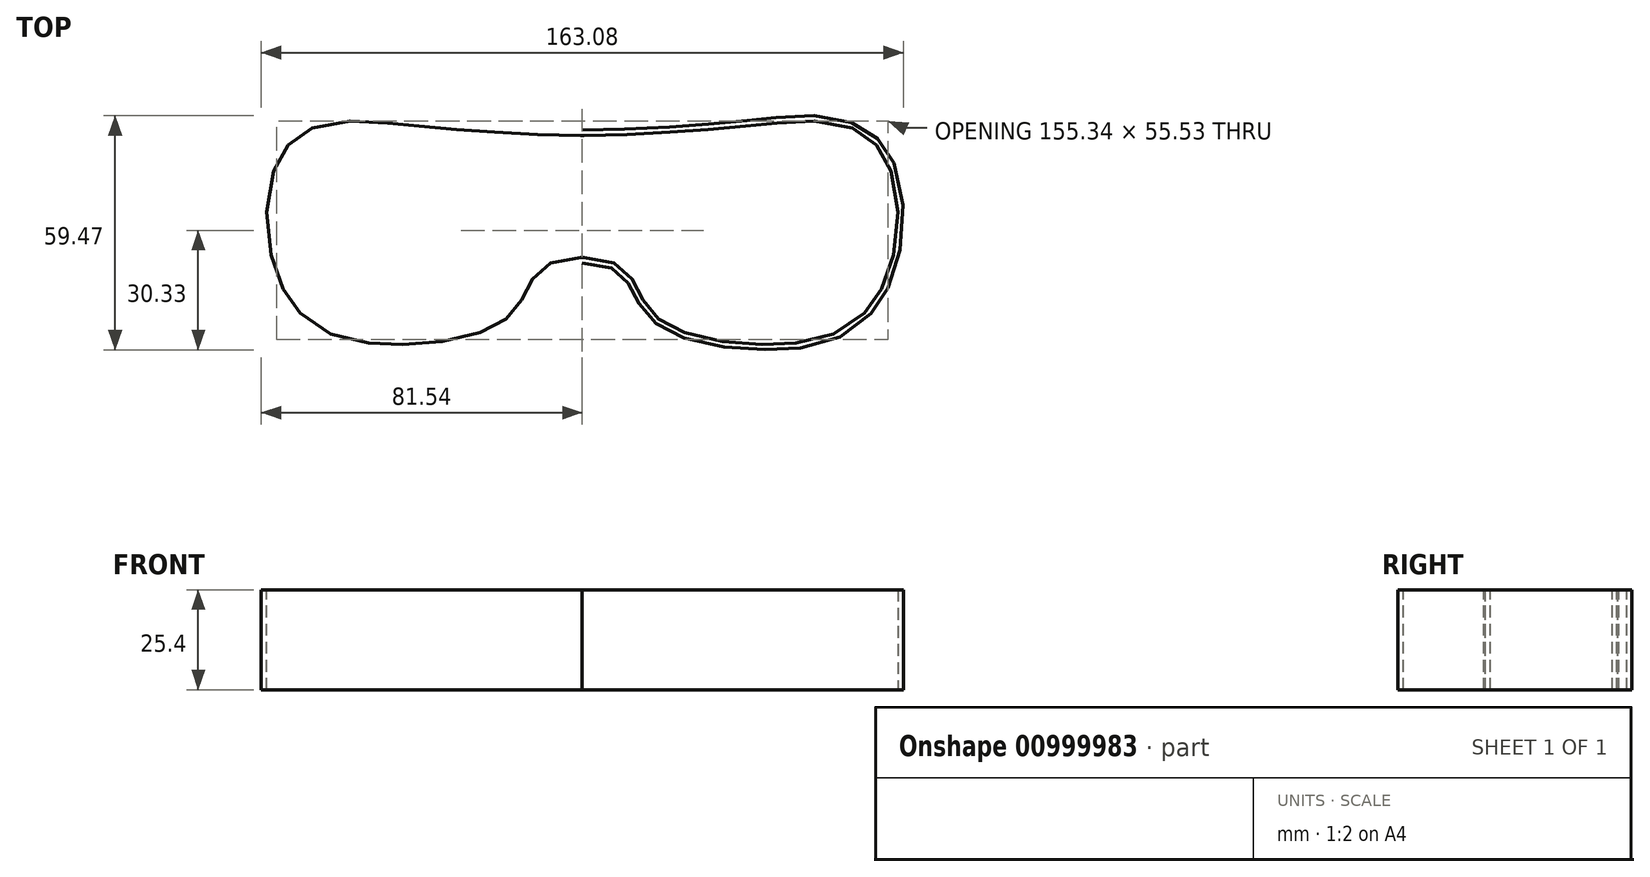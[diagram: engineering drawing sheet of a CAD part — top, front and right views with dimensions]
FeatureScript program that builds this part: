
annotation { "Feature Type Name" : "Feature", "Feature Type Description" : "" }
export const myFeature = defineFeature(function(context is Context, id is Id, definition is map)
    precondition{}
    {
        {
            var Q0;
            Q0=qCreatedBy(makeId("Top.planeOp"),FACE);
            var sketch = newSketch(context, id + "F0", { "sketchPlane" : qUnion([Q0])});
            skFitSpline(sketch, "E0", {"points": [v(0, 38) * mm, v(-24.8, 39) * mm, v(-48.12, 41) * mm, v(-71.12, 37) * mm, v(-71, 5.27) * mm, v(-50, -5) * mm, v(-23, 0) * mm, v(-17.5, 8.2) * mm, v(0, 17) * mm], "startDerivative": vector(-158.49, 0) * mm, "endDerivative": vector(270.62, 0) * mm});
            skLineSegment(sketch, "E1", {"start": v(0, 66.36) * mm, "end": v(0, -18.62) * mm, "construction": true});
            skFitSpline(sketch, "E2.MirrorCS", {"points": [v(0, 38) * mm, v(24.8, 39) * mm, v(48.12, 41) * mm, v(71.12, 37) * mm, v(71, 5.27) * mm, v(50, -5) * mm, v(23, 0) * mm, v(17.5, 8.2) * mm, v(0, 17) * mm], "startDerivative": vector(158.49, 0) * mm, "endDerivative": vector(-270.62, 0) * mm});
            skFitSpline(sketch, "E3.0", {"points": [v(0, 33.94) * mm, v(-1.7, 33.94) * mm, v(-5.35, 33.99) * mm, v(-11.39, 34.19) * mm, v(-16.62, 34.44) * mm, v(-20.79, 34.67) * mm, v(-23.86, 34.86) * mm, v(-26.84, 35.06) * mm, v(-30.69, 35.34) * mm, v(-35.35, 35.72) * mm, v(-40, 36.14) * mm, v(-43.82, 36.5) * mm, v(-46.28, 36.74) * mm, v(-48.3, 36.93) * mm, v(-50.35, 37.14) * mm, v(-52.92, 37.38) * mm, v(-55.94, 37.56) * mm, v(-58.82, 37.59) * mm, v(-61.47, 37.4) * mm, v(-63.8, 36.94) * mm, v(-65.38, 36.35) * mm, v(-66.44, 35.76) * mm, v(-67.14, 35.26) * mm, v(-67.66, 34.78) * mm, v(-68.05, 34.35) * mm, v(-68.42, 33.87) * mm, v(-68.88, 33.17) * mm, v(-69.56, 31.83) * mm, v(-70.27, 29.78) * mm, v(-70.85, 26.85) * mm, v(-71.1, 23.61) * mm, v(-71.03, 20.2) * mm, v(-70.63, 16.77) * mm, v(-69.94, 13.46) * mm, v(-68.98, 10.4) * mm, v(-67.99, 8.18) * mm, v(-67.12, 6.68) * mm, v(-66.2, 5.33) * mm, v(-64.95, 3.91) * mm, v(-63.26, 2.54) * mm, v(-61.35, 1.42) * mm, v(-59.18, 0.53) * mm, v(-56.74, -0.14) * mm, v(-54.03, -0.62) * mm, v(-51.07, -0.9) * mm, v(-47.87, -1.02) * mm, v(-44.56, -1) * mm, v(-41.22, -0.8) * mm, v(-37.93, -0.46) * mm, v(-34.78, 0.03) * mm, v(-31.87, 0.66) * mm, v(-29.28, 1.41) * mm, v(-27.48, 2.12) * mm, v(-26.33, 2.7) * mm, v(-25.61, 3.12) * mm, v(-25.07, 3.51) * mm, v(-24.48, 4.04) * mm, v(-23.89, 4.75) * mm, v(-23.22, 5.85) * mm, v(-22.5, 7.3) * mm, v(-21.8, 8.8) * mm, v(-21.08, 10.13) * mm, v(-20.26, 11.52) * mm, v(-19.01, 13.29) * mm, v(-17.09, 15.36) * mm, v(-14.7, 17.27) * mm, v(-11.8, 18.89) * mm, v(-8.4, 20.11) * mm, v(-4.5, 20.88) * mm, v(-1.57, 21.06) * mm, v(0, 21.06) * mm, v(0, 33.94) * mm]});
            skFitSpline(sketch, "E3.1", {"points": [v(0, 33.94) * mm, v(1.7, 33.94) * mm, v(5.35, 33.99) * mm, v(11.39, 34.19) * mm, v(16.62, 34.44) * mm, v(20.79, 34.67) * mm, v(23.86, 34.86) * mm, v(26.84, 35.06) * mm, v(30.69, 35.34) * mm, v(35.35, 35.72) * mm, v(40, 36.14) * mm, v(43.82, 36.5) * mm, v(46.28, 36.74) * mm, v(48.3, 36.93) * mm, v(50.35, 37.14) * mm, v(52.92, 37.38) * mm, v(55.94, 37.56) * mm, v(58.82, 37.59) * mm, v(61.47, 37.4) * mm, v(63.8, 36.94) * mm, v(65.38, 36.35) * mm, v(66.44, 35.76) * mm, v(67.14, 35.26) * mm, v(67.66, 34.78) * mm, v(68.05, 34.35) * mm, v(68.42, 33.87) * mm, v(68.88, 33.17) * mm, v(69.56, 31.83) * mm, v(70.27, 29.78) * mm, v(70.85, 26.85) * mm, v(71.1, 23.61) * mm, v(71.03, 20.2) * mm, v(70.63, 16.77) * mm, v(69.94, 13.46) * mm, v(68.98, 10.4) * mm, v(67.99, 8.18) * mm, v(67.12, 6.68) * mm, v(66.2, 5.33) * mm, v(64.95, 3.91) * mm, v(63.26, 2.54) * mm, v(61.35, 1.42) * mm, v(59.18, 0.53) * mm, v(56.74, -0.14) * mm, v(54.03, -0.62) * mm, v(51.07, -0.9) * mm, v(47.87, -1.02) * mm, v(44.56, -1) * mm, v(41.22, -0.8) * mm, v(37.93, -0.46) * mm, v(34.78, 0.03) * mm, v(31.87, 0.66) * mm, v(29.28, 1.41) * mm, v(27.48, 2.12) * mm, v(26.33, 2.7) * mm, v(25.61, 3.12) * mm, v(25.07, 3.51) * mm, v(24.48, 4.04) * mm, v(23.89, 4.75) * mm, v(23.22, 5.85) * mm, v(22.5, 7.3) * mm, v(21.8, 8.8) * mm, v(21.08, 10.13) * mm, v(20.26, 11.52) * mm, v(19.01, 13.29) * mm, v(17.09, 15.36) * mm, v(14.7, 17.27) * mm, v(11.8, 18.89) * mm, v(8.4, 20.11) * mm, v(4.5, 20.88) * mm, v(1.57, 21.06) * mm, v(0, 21.06) * mm, v(0, 33.94) * mm]});
            skFitSpline(sketch, "E4.0", {"points": [v(0, 33.94) * mm, v(-1.7, 33.94) * mm, v(-5.35, 33.99) * mm, v(-11.39, 34.19) * mm, v(-16.62, 34.44) * mm, v(-20.79, 34.67) * mm, v(-23.86, 34.86) * mm, v(-26.84, 35.06) * mm, v(-30.69, 35.34) * mm, v(-35.35, 35.72) * mm, v(-40, 36.14) * mm, v(-43.82, 36.5) * mm, v(-46.28, 36.74) * mm, v(-48.3, 36.93) * mm, v(-50.35, 37.14) * mm, v(-52.92, 37.38) * mm, v(-55.94, 37.56) * mm, v(-58.82, 37.59) * mm, v(-61.47, 37.4) * mm, v(-63.8, 36.94) * mm, v(-65.38, 36.35) * mm, v(-66.44, 35.76) * mm, v(-67.14, 35.26) * mm, v(-67.66, 34.78) * mm, v(-68.05, 34.35) * mm, v(-68.42, 33.87) * mm, v(-68.88, 33.17) * mm, v(-69.56, 31.83) * mm, v(-70.27, 29.78) * mm, v(-70.85, 26.85) * mm, v(-71.1, 23.61) * mm, v(-71.03, 20.2) * mm, v(-70.63, 16.77) * mm, v(-69.94, 13.46) * mm, v(-68.98, 10.4) * mm, v(-67.99, 8.18) * mm, v(-67.12, 6.68) * mm, v(-66.2, 5.33) * mm, v(-64.95, 3.91) * mm, v(-63.26, 2.54) * mm, v(-61.35, 1.42) * mm, v(-59.18, 0.53) * mm, v(-56.74, -0.14) * mm, v(-54.03, -0.62) * mm, v(-51.07, -0.9) * mm, v(-47.87, -1.02) * mm, v(-44.56, -1) * mm, v(-41.22, -0.8) * mm, v(-37.93, -0.46) * mm, v(-34.78, 0.03) * mm, v(-31.87, 0.66) * mm, v(-29.28, 1.41) * mm, v(-27.48, 2.12) * mm, v(-26.33, 2.7) * mm, v(-25.61, 3.12) * mm, v(-25.07, 3.51) * mm, v(-24.48, 4.04) * mm, v(-23.89, 4.75) * mm, v(-23.22, 5.85) * mm, v(-22.5, 7.3) * mm, v(-21.8, 8.8) * mm, v(-21.08, 10.13) * mm, v(-20.26, 11.52) * mm, v(-19.01, 13.29) * mm, v(-17.09, 15.36) * mm, v(-14.7, 17.27) * mm, v(-11.8, 18.89) * mm, v(-8.4, 20.11) * mm, v(-4.5, 20.88) * mm, v(-1.57, 21.06) * mm, v(0, 21.06) * mm, v(0, 33.94) * mm]});
            skFitSpline(sketch, "E4.1", {"points": [v(0, 33.94) * mm, v(1.7, 33.94) * mm, v(5.35, 33.99) * mm, v(11.39, 34.19) * mm, v(16.62, 34.44) * mm, v(20.79, 34.67) * mm, v(23.86, 34.86) * mm, v(26.84, 35.06) * mm, v(30.69, 35.34) * mm, v(35.35, 35.72) * mm, v(40, 36.14) * mm, v(43.82, 36.5) * mm, v(46.28, 36.74) * mm, v(48.3, 36.93) * mm, v(50.35, 37.14) * mm, v(52.92, 37.38) * mm, v(55.94, 37.56) * mm, v(58.82, 37.59) * mm, v(61.47, 37.4) * mm, v(63.8, 36.94) * mm, v(65.38, 36.35) * mm, v(66.44, 35.76) * mm, v(67.14, 35.26) * mm, v(67.66, 34.78) * mm, v(68.05, 34.35) * mm, v(68.42, 33.87) * mm, v(68.88, 33.17) * mm, v(69.56, 31.83) * mm, v(70.27, 29.78) * mm, v(70.85, 26.85) * mm, v(71.1, 23.61) * mm, v(71.03, 20.2) * mm, v(70.63, 16.77) * mm, v(69.94, 13.46) * mm, v(68.98, 10.4) * mm, v(67.99, 8.18) * mm, v(67.12, 6.68) * mm, v(66.2, 5.33) * mm, v(64.95, 3.91) * mm, v(63.26, 2.54) * mm, v(61.35, 1.42) * mm, v(59.18, 0.53) * mm, v(56.74, -0.14) * mm, v(54.03, -0.62) * mm, v(51.07, -0.9) * mm, v(47.87, -1.02) * mm, v(44.56, -1) * mm, v(41.22, -0.8) * mm, v(37.93, -0.46) * mm, v(34.78, 0.03) * mm, v(31.87, 0.66) * mm, v(29.28, 1.41) * mm, v(27.48, 2.12) * mm, v(26.33, 2.7) * mm, v(25.61, 3.12) * mm, v(25.07, 3.51) * mm, v(24.48, 4.04) * mm, v(23.89, 4.75) * mm, v(23.22, 5.85) * mm, v(22.5, 7.3) * mm, v(21.8, 8.8) * mm, v(21.08, 10.13) * mm, v(20.26, 11.52) * mm, v(19.01, 13.29) * mm, v(17.09, 15.36) * mm, v(14.7, 17.27) * mm, v(11.8, 18.89) * mm, v(8.4, 20.11) * mm, v(4.5, 20.88) * mm, v(1.57, 21.06) * mm, v(0, 21.06) * mm, v(0, 33.94) * mm]});
            skFitSpline(sketch, "E5.0", {"points": [v(0, 44.35) * mm, v(-1.59, 44.35) * mm, v(-5.09, 44.4) * mm, v(-10.96, 44.6) * mm, v(-16.09, 44.84) * mm, v(-20.17, 45.07) * mm, v(-23.2, 45.26) * mm, v(-26.12, 45.45) * mm, v(-29.89, 45.73) * mm, v(-33.55, 46.02) * mm, v(-37.21, 46.34) * mm, v(-39.99, 46.6) * mm, v(-42.83, 46.86) * mm, v(-45.26, 47.1) * mm, v(-47.02, 47.27) * mm, v(-48.04, 47.37) * mm, v(-49.61, 47.53) * mm, v(-52.07, 47.76) * mm, v(-55.53, 47.97) * mm, v(-59.1, 48) * mm, v(-62.76, 47.75) * mm, v(-65.86, 47.16) * mm, v(-68.34, 46.37) * mm, v(-70.19, 45.6) * mm, v(-72, 44.6) * mm, v(-73.73, 43.36) * mm, v(-75.06, 42.13) * mm, v(-76.05, 41.02) * mm, v(-76.96, 39.85) * mm, v(-77.94, 38.33) * mm, v(-79.23, 35.77) * mm, v(-80.38, 32.41) * mm, v(-81.2, 28.2) * mm, v(-81.53, 23.87) * mm, v(-81.43, 19.5) * mm, v(-80.93, 15.13) * mm, v(-80.04, 10.86) * mm, v(-78.97, 7.44) * mm, v(-77.9, 4.83) * mm, v(-77, 2.94) * mm, v(-75.95, 1.13) * mm, v(-74.8, -0.55) * mm, v(-73.53, -2.12) * mm, v(-71.7, -4.02) * mm, v(-69.2, -6.07) * mm, v(-65.93, -7.97) * mm, v(-62.5, -9.37) * mm, v(-58.97, -10.33) * mm, v(-55.37, -10.95) * mm, v(-52.33, -11.24) * mm, v(-49.87, -11.37) * mm, v(-47.38, -11.43) * mm, v(-44.22, -11.4) * mm, v(-40.4, -11.19) * mm, v(-36.6, -10.8) * mm, v(-32.9, -10.22) * mm, v(-29.36, -9.46) * mm, v(-26, -8.48) * mm, v(-23.36, -7.46) * mm, v(-21.37, -6.47) * mm, v(-19.93, -5.63) * mm, v(-18.55, -4.62) * mm, v(-17.32, -3.54) * mm, v(-16.27, -2.4) * mm, v(-15.38, -1.23) * mm, v(-14.64, -0.1) * mm, v(-13.83, 1.32) * mm, v(-13.07, 2.9) * mm, v(-12.46, 4.17) * mm, v(-12.06, 4.92) * mm, v(-11.83, 5.32) * mm, v(-11.59, 5.7) * mm, v(-11.27, 6.18) * mm, v(-10.73, 6.89) * mm, v(-9.98, 7.7) * mm, v(-8.89, 8.57) * mm, v(-7.5, 9.35) * mm, v(-5.66, 10.02) * mm, v(-3.24, 10.52) * mm, v(-1.17, 10.65) * mm, v(0, 10.65) * mm, v(0, 44.35) * mm]});
            skFitSpline(sketch, "E5.1", {"points": [v(0, 44.35) * mm, v(1.59, 44.35) * mm, v(5.09, 44.4) * mm, v(10.96, 44.6) * mm, v(16.09, 44.84) * mm, v(20.17, 45.07) * mm, v(23.2, 45.26) * mm, v(26.12, 45.45) * mm, v(29.89, 45.73) * mm, v(33.55, 46.02) * mm, v(37.21, 46.34) * mm, v(39.99, 46.6) * mm, v(42.83, 46.86) * mm, v(45.26, 47.1) * mm, v(47.02, 47.27) * mm, v(48.04, 47.37) * mm, v(49.61, 47.53) * mm, v(52.07, 47.76) * mm, v(55.53, 47.97) * mm, v(59.1, 48) * mm, v(62.76, 47.75) * mm, v(65.86, 47.16) * mm, v(68.34, 46.37) * mm, v(70.19, 45.6) * mm, v(72, 44.6) * mm, v(73.73, 43.36) * mm, v(75.06, 42.13) * mm, v(76.05, 41.02) * mm, v(76.96, 39.85) * mm, v(77.94, 38.33) * mm, v(79.23, 35.77) * mm, v(80.38, 32.41) * mm, v(81.2, 28.2) * mm, v(81.53, 23.87) * mm, v(81.43, 19.5) * mm, v(80.93, 15.13) * mm, v(80.04, 10.86) * mm, v(78.97, 7.44) * mm, v(77.9, 4.83) * mm, v(77, 2.94) * mm, v(75.95, 1.13) * mm, v(74.8, -0.55) * mm, v(73.53, -2.12) * mm, v(71.7, -4.02) * mm, v(69.2, -6.07) * mm, v(65.93, -7.97) * mm, v(62.5, -9.37) * mm, v(58.97, -10.33) * mm, v(55.37, -10.95) * mm, v(52.33, -11.24) * mm, v(49.87, -11.37) * mm, v(47.38, -11.43) * mm, v(44.22, -11.4) * mm, v(40.4, -11.19) * mm, v(36.6, -10.8) * mm, v(32.9, -10.22) * mm, v(29.36, -9.46) * mm, v(26, -8.48) * mm, v(23.36, -7.46) * mm, v(21.37, -6.47) * mm, v(19.93, -5.63) * mm, v(18.55, -4.62) * mm, v(17.32, -3.54) * mm, v(16.27, -2.4) * mm, v(15.38, -1.23) * mm, v(14.64, -0.1) * mm, v(13.83, 1.32) * mm, v(13.07, 2.9) * mm, v(12.46, 4.17) * mm, v(12.06, 4.92) * mm, v(11.83, 5.32) * mm, v(11.59, 5.7) * mm, v(11.27, 6.18) * mm, v(10.73, 6.89) * mm, v(9.98, 7.7) * mm, v(8.89, 8.57) * mm, v(7.5, 9.35) * mm, v(5.66, 10.02) * mm, v(3.24, 10.52) * mm, v(1.17, 10.65) * mm, v(0, 10.65) * mm, v(0, 44.35) * mm]});
            skFitSpline(sketch, "E6.0", {"points": [v(0, 43) * mm, v(-1.6, 43) * mm, v(-5.12, 43.05) * mm, v(-11.01, 43.25) * mm, v(-16.16, 43.5) * mm, v(-20.25, 43.72) * mm, v(-23.28, 43.9) * mm, v(-26.2, 44.1) * mm, v(-30, 44.38) * mm, v(-33.66, 44.68) * mm, v(-37.33, 45) * mm, v(-40.11, 45.25) * mm, v(-42.96, 45.52) * mm, v(-45.4, 45.76) * mm, v(-47.4, 45.95) * mm, v(-49.47, 46.16) * mm, v(-52.18, 46.41) * mm, v(-55.58, 46.63) * mm, v(-59.06, 46.66) * mm, v(-62.6, 46.4) * mm, v(-66.13, 45.73) * mm, v(-69.04, 44.68) * mm, v(-71.28, 43.45) * mm, v(-72.87, 42.31) * mm, v(-74.1, 41.17) * mm, v(-75.02, 40.15) * mm, v(-75.86, 39.08) * mm, v(-76.77, 37.66) * mm, v(-77.98, 35.26) * mm, v(-79.07, 32.07) * mm, v(-79.85, 28.03) * mm, v(-80.17, 23.84) * mm, v(-80.08, 19.58) * mm, v(-79.6, 15.34) * mm, v(-78.73, 11.2) * mm, v(-77.7, 7.9) * mm, v(-76.67, 5.38) * mm, v(-75.8, 3.57) * mm, v(-74.8, 1.85) * mm, v(-73.71, 0.25) * mm, v(-72.52, -1.22) * mm, v(-70.8, -3.02) * mm, v(-68.43, -4.95) * mm, v(-65.34, -6.75) * mm, v(-62.07, -8.08) * mm, v(-58.68, -9.01) * mm, v(-55.2, -9.61) * mm, v(-52.23, -9.9) * mm, v(-49.82, -10.02) * mm, v(-47.37, -10.08) * mm, v(-44.26, -10.05) * mm, v(-40.5, -9.84) * mm, v(-36.78, -9.45) * mm, v(-33.15, -8.9) * mm, v(-29.68, -8.15) * mm, v(-26.42, -7.2) * mm, v(-23.9, -6.22) * mm, v(-22.01, -5.29) * mm, v(-20.67, -4.5) * mm, v(-19.4, -3.57) * mm, v(-18.27, -2.57) * mm, v(-17.3, -1.52) * mm, v(-16.48, -0.45) * mm, v(-15.8, 0.6) * mm, v(-15.03, 1.94) * mm, v(-14.29, 3.47) * mm, v(-13.67, 4.77) * mm, v(-13.18, 5.69) * mm, v(-12.8, 6.33) * mm, v(-12.37, 6.96) * mm, v(-11.76, 7.76) * mm, v(-10.9, 8.7) * mm, v(-9.64, 9.7) * mm, v(-8.05, 10.59) * mm, v(-6.02, 11.33) * mm, v(-3.4, 11.86) * mm, v(-1.22, 12) * mm, v(0, 12) * mm]});
            skFitSpline(sketch, "E6.1", {"points": [v(0, 43) * mm, v(1.6, 43) * mm, v(5.12, 43.05) * mm, v(11.01, 43.25) * mm, v(16.16, 43.5) * mm, v(20.25, 43.72) * mm, v(23.28, 43.9) * mm, v(26.2, 44.1) * mm, v(30, 44.38) * mm, v(33.66, 44.68) * mm, v(37.33, 45) * mm, v(40.11, 45.25) * mm, v(42.96, 45.52) * mm, v(45.4, 45.76) * mm, v(47.4, 45.95) * mm, v(49.47, 46.16) * mm, v(52.18, 46.41) * mm, v(55.58, 46.63) * mm, v(59.06, 46.66) * mm, v(62.6, 46.4) * mm, v(66.13, 45.73) * mm, v(69.04, 44.68) * mm, v(71.28, 43.45) * mm, v(72.87, 42.31) * mm, v(74.1, 41.17) * mm, v(75.02, 40.15) * mm, v(75.86, 39.08) * mm, v(76.77, 37.66) * mm, v(77.98, 35.26) * mm, v(79.07, 32.07) * mm, v(79.85, 28.03) * mm, v(80.17, 23.84) * mm, v(80.08, 19.58) * mm, v(79.6, 15.34) * mm, v(78.73, 11.2) * mm, v(77.7, 7.9) * mm, v(76.67, 5.38) * mm, v(75.8, 3.57) * mm, v(74.8, 1.85) * mm, v(73.71, 0.25) * mm, v(72.52, -1.22) * mm, v(70.8, -3.02) * mm, v(68.43, -4.95) * mm, v(65.34, -6.75) * mm, v(62.07, -8.08) * mm, v(58.68, -9.01) * mm, v(55.2, -9.61) * mm, v(52.23, -9.9) * mm, v(49.82, -10.02) * mm, v(47.37, -10.08) * mm, v(44.26, -10.05) * mm, v(40.5, -9.84) * mm, v(36.78, -9.45) * mm, v(33.15, -8.9) * mm, v(29.68, -8.15) * mm, v(26.42, -7.2) * mm, v(23.9, -6.22) * mm, v(22.01, -5.29) * mm, v(20.67, -4.5) * mm, v(19.4, -3.57) * mm, v(18.27, -2.57) * mm, v(17.3, -1.52) * mm, v(16.48, -0.45) * mm, v(15.8, 0.6) * mm, v(15.03, 1.94) * mm, v(14.29, 3.47) * mm, v(13.67, 4.77) * mm, v(13.18, 5.69) * mm, v(12.8, 6.33) * mm, v(12.37, 6.96) * mm, v(11.76, 7.76) * mm, v(10.9, 8.7) * mm, v(9.64, 9.7) * mm, v(8.05, 10.59) * mm, v(6.02, 11.33) * mm, v(3.4, 11.86) * mm, v(1.22, 12) * mm, v(0, 12) * mm]});
            skLineSegment(sketch, "E7", {"start": v(-10.53, 17) * mm, "end": v(10.53, 17) * mm, "construction": true});
            skSolve(sketch);
        }
        {
            var Q0;
            Q0 = qSketchRegion(id + "F0", true);
            extrude(context, id + "F1", {"entities" : qUnion([Q0]), "depth" : 25.4 * mm, "offsetDistance" : 25.4 * mm});
        }
    });
